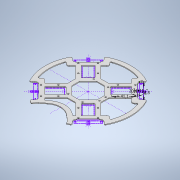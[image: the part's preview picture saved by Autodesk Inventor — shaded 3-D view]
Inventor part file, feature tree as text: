
AUTODESK INVENTOR PART (.ipt)
format: ipt  version: 2020 (Build 240168000, 168)  size: 595,456 bytes
history: native  units: mm
features: sketch x3, other x2, extrude x2, projected_geometry x1
ambient origin geometry x8: Origin, YZ Plane, XZ Plane, XY Plane, X Axis, Y Axis, Z Axis, Center Point
bodies: Body1 (feature_tree)
feature tree (8):
  other  "Твердое тело1"
  sketch  "Эскиз1"
  sketch  "Эскиз2"
  extrude  "Выдавливание1"  Depth=20.0mm
  sketch  "Эскиз3"
  other  "моторы"
  extrude  "Выдавливание2"  Depth=20.0mm
  projected_geometry  "Спроецированная петля1"
